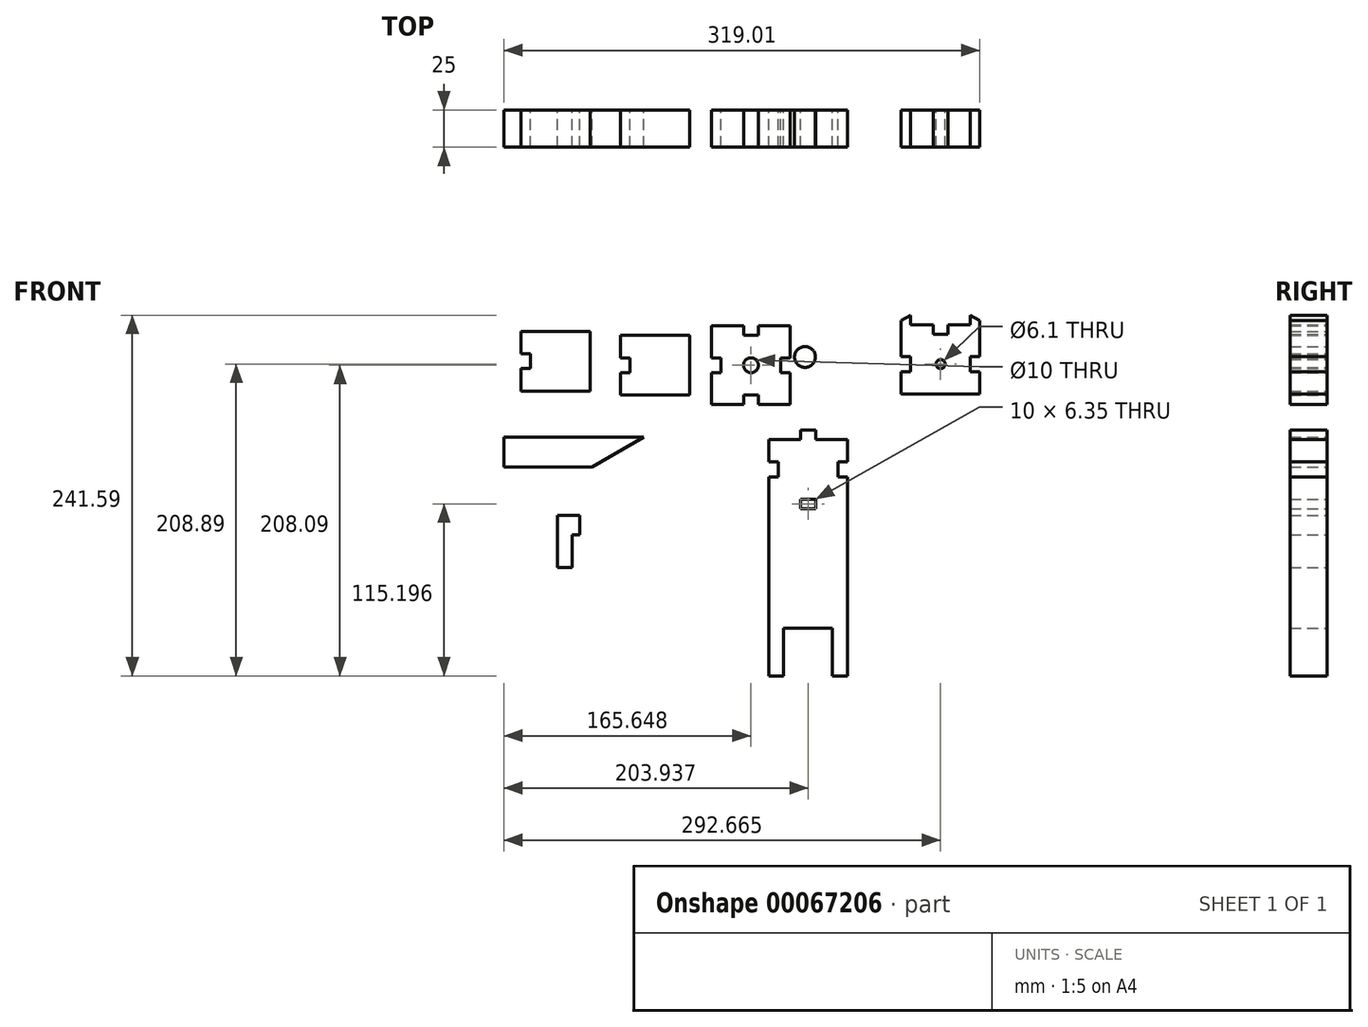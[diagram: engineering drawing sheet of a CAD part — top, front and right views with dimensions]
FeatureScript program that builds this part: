
annotation { "Feature Type Name" : "Feature", "Feature Type Description" : "" }
export const myFeature = defineFeature(function(context is Context, id is Id, definition is map)
    precondition{}
    {
        {
            var Q0;
            Q0=qCreatedBy(makeId("Front.planeOp"),FACE);
            var sketch = newSketch(context, id + "F0", { "sketchPlane" : qUnion([Q0])});
            skLineSegment(sketch, "E0.bottom", {"start": v(-118.5, 6.97) * mm, "end": v(-158.5, 6.97) * mm});
            skLineSegment(sketch, "E0.top", {"start": v(-118.5, 46.97) * mm, "end": v(-158.5, 46.97) * mm});
            skLineSegment(sketch, "E0.left", {"start": v(-118.5, 6.97) * mm, "end": v(-118.5, 46.97) * mm});
            skLineSegment(sketch, "E0.right", {"start": v(-158.5, 6.97) * mm, "end": v(-158.5, 46.97) * mm});
            skPoint(sketch, "E0.middle", {"position": v(-138.5, 26.97) * mm});
            skLineSegment(sketch, "E1.bottom", {"start": v(-112.15, 0.62) * mm, "end": v(-164.85, 0.62) * mm});
            skLineSegment(sketch, "E1.top", {"start": v(-112.15, 53.32) * mm, "end": v(-164.85, 53.32) * mm});
            skLineSegment(sketch, "E1.left", {"start": v(-112.15, 0.62) * mm, "end": v(-112.15, 53.32) * mm});
            skLineSegment(sketch, "E1.right", {"start": v(-164.85, 0.62) * mm, "end": v(-164.85, 53.32) * mm});
            skLineSegment(sketch, "E2.bottom", {"start": v(-133.5, 53.32) * mm, "end": v(-143.5, 53.32) * mm});
            skLineSegment(sketch, "E2.top", {"start": v(-133.5, 40.62) * mm, "end": v(-143.5, 40.62) * mm});
            skLineSegment(sketch, "E2.left", {"start": v(-133.5, 53.32) * mm, "end": v(-133.5, 40.62) * mm});
            skLineSegment(sketch, "E2.right", {"start": v(-143.5, 53.32) * mm, "end": v(-143.5, 40.62) * mm});
            skPoint(sketch, "E2.middle", {"position": v(-138.5, 46.97) * mm});
            skLineSegment(sketch, "E3.bottom", {"start": v(-112.15, 31.97) * mm, "end": v(-124.85, 31.97) * mm});
            skLineSegment(sketch, "E3.top", {"start": v(-112.15, 21.97) * mm, "end": v(-124.85, 21.97) * mm});
            skLineSegment(sketch, "E3.left", {"start": v(-112.15, 31.97) * mm, "end": v(-112.15, 21.97) * mm});
            skLineSegment(sketch, "E3.right", {"start": v(-124.85, 31.97) * mm, "end": v(-124.85, 21.97) * mm});
            skPoint(sketch, "E3.middle", {"position": v(-118.5, 26.97) * mm});
            skLineSegment(sketch, "E4.bottom", {"start": v(-133.5, 0.62) * mm, "end": v(-143.5, 0.62) * mm});
            skLineSegment(sketch, "E4.top", {"start": v(-133.5, 13.32) * mm, "end": v(-143.5, 13.32) * mm});
            skLineSegment(sketch, "E4.left", {"start": v(-133.5, 0.62) * mm, "end": v(-133.5, 13.32) * mm});
            skLineSegment(sketch, "E4.right", {"start": v(-143.5, 0.62) * mm, "end": v(-143.5, 13.32) * mm});
            skPoint(sketch, "E4.middle", {"position": v(-138.5, 6.97) * mm});
            skLineSegment(sketch, "E5.bottom", {"start": v(-164.85, 31.97) * mm, "end": v(-152.15, 31.97) * mm});
            skLineSegment(sketch, "E5.top", {"start": v(-164.85, 21.97) * mm, "end": v(-152.15, 21.97) * mm});
            skLineSegment(sketch, "E5.left", {"start": v(-164.85, 31.97) * mm, "end": v(-164.85, 21.97) * mm});
            skLineSegment(sketch, "E5.right", {"start": v(-152.15, 31.97) * mm, "end": v(-152.15, 21.97) * mm});
            skPoint(sketch, "E5.middle", {"position": v(-158.5, 26.97) * mm});
            skLineSegment(sketch, "E6", {"start": v(-158.5, 46.97) * mm, "end": v(-158.5, 53.32) * mm});
            skLineSegment(sketch, "E7", {"start": v(-158.5, 46.97) * mm, "end": v(-164.85, 46.97) * mm});
            skLineSegment(sketch, "E8", {"start": v(-158.5, 6.97) * mm, "end": v(-164.85, 6.97) * mm});
            skLineSegment(sketch, "E9", {"start": v(-158.5, 6.97) * mm, "end": v(-158.5, 0.62) * mm});
            skLineSegment(sketch, "E10", {"start": v(-118.5, 6.97) * mm, "end": v(-118.5, 0.62) * mm});
            skLineSegment(sketch, "E11", {"start": v(-118.5, 6.97) * mm, "end": v(-112.15, 6.97) * mm});
            skLineSegment(sketch, "E12", {"start": v(-118.5, 46.97) * mm, "end": v(-112.15, 46.97) * mm});
            skLineSegment(sketch, "E13", {"start": v(-118.5, 46.97) * mm, "end": v(-118.5, 53.32) * mm});
            skLineSegment(sketch, "E14.bottom", {"start": v(-51.59, 4.22) * mm, "end": v(-91.59, 4.22) * mm});
            skLineSegment(sketch, "E14.top", {"start": v(-51.59, 44.22) * mm, "end": v(-91.59, 44.22) * mm});
            skLineSegment(sketch, "E14.left", {"start": v(-51.59, 4.22) * mm, "end": v(-51.59, 44.22) * mm});
            skLineSegment(sketch, "E14.right", {"start": v(-91.59, 4.22) * mm, "end": v(-91.59, 44.22) * mm});
            skPoint(sketch, "E14.middle", {"position": v(-71.59, 24.22) * mm});
            skLineSegment(sketch, "E15.bottom", {"start": v(-45.24, -2.13) * mm, "end": v(-97.94, -2.13) * mm});
            skLineSegment(sketch, "E15.top", {"start": v(-45.24, 50.57) * mm, "end": v(-97.94, 50.57) * mm});
            skLineSegment(sketch, "E15.left", {"start": v(-45.24, -2.13) * mm, "end": v(-45.24, 50.57) * mm});
            skLineSegment(sketch, "E15.right", {"start": v(-97.94, -2.13) * mm, "end": v(-97.94, 50.57) * mm});
            skLineSegment(sketch, "E16.bottom", {"start": v(-66.59, 50.57) * mm, "end": v(-76.59, 50.57) * mm});
            skLineSegment(sketch, "E16.top", {"start": v(-66.59, 37.87) * mm, "end": v(-76.59, 37.87) * mm});
            skLineSegment(sketch, "E16.left", {"start": v(-66.59, 50.57) * mm, "end": v(-66.59, 37.87) * mm});
            skLineSegment(sketch, "E16.right", {"start": v(-76.59, 50.57) * mm, "end": v(-76.59, 37.87) * mm});
            skPoint(sketch, "E16.middle", {"position": v(-71.59, 44.22) * mm});
            skLineSegment(sketch, "E17.bottom", {"start": v(-45.24, 29.22) * mm, "end": v(-57.94, 29.22) * mm});
            skLineSegment(sketch, "E17.top", {"start": v(-45.24, 19.22) * mm, "end": v(-57.94, 19.22) * mm});
            skLineSegment(sketch, "E17.left", {"start": v(-45.24, 29.22) * mm, "end": v(-45.24, 19.22) * mm});
            skLineSegment(sketch, "E17.right", {"start": v(-57.94, 29.22) * mm, "end": v(-57.94, 19.22) * mm});
            skPoint(sketch, "E17.middle", {"position": v(-51.59, 24.22) * mm});
            skLineSegment(sketch, "E18.bottom", {"start": v(-66.59, -2.13) * mm, "end": v(-76.59, -2.13) * mm});
            skLineSegment(sketch, "E18.top", {"start": v(-66.59, 10.57) * mm, "end": v(-76.59, 10.57) * mm});
            skLineSegment(sketch, "E18.left", {"start": v(-66.59, -2.13) * mm, "end": v(-66.59, 10.57) * mm});
            skLineSegment(sketch, "E18.right", {"start": v(-76.59, -2.13) * mm, "end": v(-76.59, 10.57) * mm});
            skPoint(sketch, "E18.middle", {"position": v(-71.59, 4.22) * mm});
            skLineSegment(sketch, "E19.bottom", {"start": v(-97.94, 29.22) * mm, "end": v(-85.24, 29.22) * mm});
            skLineSegment(sketch, "E19.top", {"start": v(-97.94, 19.22) * mm, "end": v(-85.24, 19.22) * mm});
            skLineSegment(sketch, "E19.left", {"start": v(-97.94, 29.22) * mm, "end": v(-97.94, 19.22) * mm});
            skLineSegment(sketch, "E19.right", {"start": v(-85.24, 29.22) * mm, "end": v(-85.24, 19.22) * mm});
            skPoint(sketch, "E19.middle", {"position": v(-91.59, 24.22) * mm});
            skLineSegment(sketch, "E20", {"start": v(-91.59, 44.22) * mm, "end": v(-91.59, 50.57) * mm});
            skLineSegment(sketch, "E21", {"start": v(-91.59, 44.22) * mm, "end": v(-97.94, 44.22) * mm});
            skLineSegment(sketch, "E22", {"start": v(-91.59, 4.22) * mm, "end": v(-97.94, 4.22) * mm});
            skLineSegment(sketch, "E23", {"start": v(-91.59, 4.22) * mm, "end": v(-91.59, -2.13) * mm});
            skLineSegment(sketch, "E24", {"start": v(-51.59, 4.22) * mm, "end": v(-51.59, -2.13) * mm});
            skLineSegment(sketch, "E25", {"start": v(-51.59, 4.22) * mm, "end": v(-45.24, 4.22) * mm});
            skLineSegment(sketch, "E26", {"start": v(-51.59, 44.22) * mm, "end": v(-45.24, 44.22) * mm});
            skLineSegment(sketch, "E27", {"start": v(-51.59, 44.22) * mm, "end": v(-51.59, 50.57) * mm});
            skLineSegment(sketch, "E28.bottom", {"start": v(9.4, 4.22) * mm, "end": v(-30.6, 4.22) * mm});
            skLineSegment(sketch, "E28.top", {"start": v(9.4, 44.22) * mm, "end": v(-30.6, 44.22) * mm});
            skLineSegment(sketch, "E28.left", {"start": v(9.4, 4.22) * mm, "end": v(9.4, 44.22) * mm});
            skLineSegment(sketch, "E28.right", {"start": v(-30.6, 4.22) * mm, "end": v(-30.6, 44.22) * mm});
            skPoint(sketch, "E28.middle", {"position": v(-10.6, 24.22) * mm});
            skLineSegment(sketch, "E29.bottom", {"start": v(15.75, -2.13) * mm, "end": v(-36.95, -2.13) * mm});
            skLineSegment(sketch, "E29.top", {"start": v(15.75, 50.57) * mm, "end": v(-36.95, 50.57) * mm});
            skLineSegment(sketch, "E29.left", {"start": v(15.75, -2.13) * mm, "end": v(15.75, 50.57) * mm});
            skLineSegment(sketch, "E29.right", {"start": v(-36.95, -2.13) * mm, "end": v(-36.95, 50.57) * mm});
            skLineSegment(sketch, "E30.bottom", {"start": v(-5.6, 50.57) * mm, "end": v(-15.6, 50.57) * mm});
            skLineSegment(sketch, "E30.top", {"start": v(-5.6, 37.87) * mm, "end": v(-15.6, 37.87) * mm});
            skLineSegment(sketch, "E30.left", {"start": v(-5.6, 50.57) * mm, "end": v(-5.6, 37.87) * mm});
            skLineSegment(sketch, "E30.right", {"start": v(-15.6, 50.57) * mm, "end": v(-15.6, 37.87) * mm});
            skPoint(sketch, "E30.middle", {"position": v(-10.6, 44.22) * mm});
            skLineSegment(sketch, "E31.bottom", {"start": v(15.75, 29.22) * mm, "end": v(3.05, 29.22) * mm});
            skLineSegment(sketch, "E31.top", {"start": v(15.75, 19.22) * mm, "end": v(3.05, 19.22) * mm});
            skLineSegment(sketch, "E31.left", {"start": v(15.75, 29.22) * mm, "end": v(15.75, 19.22) * mm});
            skLineSegment(sketch, "E31.right", {"start": v(3.05, 29.22) * mm, "end": v(3.05, 19.22) * mm});
            skPoint(sketch, "E31.middle", {"position": v(9.4, 24.22) * mm});
            skLineSegment(sketch, "E32.bottom", {"start": v(-5.6, -2.13) * mm, "end": v(-15.6, -2.13) * mm});
            skLineSegment(sketch, "E32.top", {"start": v(-5.6, 10.57) * mm, "end": v(-15.6, 10.57) * mm});
            skLineSegment(sketch, "E32.left", {"start": v(-5.6, -2.13) * mm, "end": v(-5.6, 10.57) * mm});
            skLineSegment(sketch, "E32.right", {"start": v(-15.6, -2.13) * mm, "end": v(-15.6, 10.57) * mm});
            skPoint(sketch, "E32.middle", {"position": v(-10.6, 4.22) * mm});
            skLineSegment(sketch, "E33.bottom", {"start": v(-36.95, 29.22) * mm, "end": v(-24.25, 29.22) * mm});
            skLineSegment(sketch, "E33.top", {"start": v(-36.95, 19.22) * mm, "end": v(-24.25, 19.22) * mm});
            skLineSegment(sketch, "E33.left", {"start": v(-36.95, 29.22) * mm, "end": v(-36.95, 19.22) * mm});
            skLineSegment(sketch, "E33.right", {"start": v(-24.25, 29.22) * mm, "end": v(-24.25, 19.22) * mm});
            skPoint(sketch, "E33.middle", {"position": v(-30.6, 24.22) * mm});
            skLineSegment(sketch, "E34", {"start": v(-30.6, 44.22) * mm, "end": v(-30.6, 50.57) * mm});
            skLineSegment(sketch, "E35", {"start": v(-30.6, 44.22) * mm, "end": v(-36.95, 44.22) * mm});
            skLineSegment(sketch, "E36", {"start": v(-30.6, 4.22) * mm, "end": v(-36.95, 4.22) * mm});
            skLineSegment(sketch, "E37", {"start": v(-30.6, 4.22) * mm, "end": v(-30.6, -2.13) * mm});
            skLineSegment(sketch, "E38", {"start": v(9.4, 4.22) * mm, "end": v(9.4, -2.13) * mm});
            skLineSegment(sketch, "E39", {"start": v(9.4, 4.22) * mm, "end": v(15.75, 4.22) * mm});
            skLineSegment(sketch, "E40", {"start": v(9.4, 44.22) * mm, "end": v(15.75, 44.22) * mm});
            skLineSegment(sketch, "E41", {"start": v(9.4, 44.22) * mm, "end": v(9.4, 50.57) * mm});
            skLineSegment(sketch, "E42.bottom", {"start": v(142.76, -1.33) * mm, "end": v(90.06, -1.33) * mm});
            skLineSegment(sketch, "E42.top", {"start": v(142.76, 51.37) * mm, "end": v(90.06, 51.37) * mm});
            skLineSegment(sketch, "E42.left", {"start": v(142.76, -1.33) * mm, "end": v(142.76, 51.37) * mm});
            skLineSegment(sketch, "E42.right", {"start": v(90.06, -1.33) * mm, "end": v(90.06, 51.37) * mm});
            skPoint(sketch, "E42.middle", {"position": v(116.41, 25.02) * mm});
            skLineSegment(sketch, "E43.bottom", {"start": v(136.41, 5.02) * mm, "end": v(96.41, 5.02) * mm});
            skLineSegment(sketch, "E43.top", {"start": v(136.41, 45.02) * mm, "end": v(96.41, 45.02) * mm});
            skLineSegment(sketch, "E43.left", {"start": v(136.41, 5.02) * mm, "end": v(136.41, 45.02) * mm});
            skLineSegment(sketch, "E43.right", {"start": v(96.41, 5.02) * mm, "end": v(96.41, 45.02) * mm});
            skLineSegment(sketch, "E44.bottom", {"start": v(121.41, 38.53) * mm, "end": v(111.41, 38.53) * mm});
            skLineSegment(sketch, "E44.top", {"start": v(121.41, 51.5) * mm, "end": v(111.41, 51.5) * mm});
            skLineSegment(sketch, "E44.left", {"start": v(121.41, 38.53) * mm, "end": v(121.41, 51.5) * mm});
            skLineSegment(sketch, "E44.right", {"start": v(111.41, 38.53) * mm, "end": v(111.41, 51.5) * mm});
            skPoint(sketch, "E44.middle", {"position": v(116.41, 45.02) * mm});
            skLineSegment(sketch, "E45.bottom", {"start": v(121.41, -1.33) * mm, "end": v(111.41, -1.33) * mm});
            skLineSegment(sketch, "E45.top", {"start": v(121.41, 11.37) * mm, "end": v(111.41, 11.37) * mm});
            skLineSegment(sketch, "E45.left", {"start": v(121.41, -1.33) * mm, "end": v(121.41, 11.37) * mm});
            skLineSegment(sketch, "E45.right", {"start": v(111.41, -1.33) * mm, "end": v(111.41, 11.37) * mm});
            skPoint(sketch, "E45.middle", {"position": v(116.41, 5.02) * mm});
            skLineSegment(sketch, "E46.bottom", {"start": v(142.76, 20.02) * mm, "end": v(130.06, 20.02) * mm});
            skLineSegment(sketch, "E46.top", {"start": v(142.76, 30.02) * mm, "end": v(130.06, 30.02) * mm});
            skLineSegment(sketch, "E46.left", {"start": v(142.76, 20.02) * mm, "end": v(142.76, 30.02) * mm});
            skLineSegment(sketch, "E46.right", {"start": v(130.06, 20.02) * mm, "end": v(130.06, 30.02) * mm});
            skPoint(sketch, "E46.middle", {"position": v(136.41, 25.02) * mm});
            skLineSegment(sketch, "E47.bottom", {"start": v(90.06, 20.02) * mm, "end": v(102.76, 20.02) * mm});
            skLineSegment(sketch, "E47.top", {"start": v(90.06, 30.02) * mm, "end": v(102.76, 30.02) * mm});
            skLineSegment(sketch, "E47.left", {"start": v(90.06, 20.02) * mm, "end": v(90.06, 30.02) * mm});
            skLineSegment(sketch, "E47.right", {"start": v(102.76, 20.02) * mm, "end": v(102.76, 30.02) * mm});
            skPoint(sketch, "E47.middle", {"position": v(96.41, 25.02) * mm});
            skLineSegment(sketch, "E48.bottom", {"start": v(90.06, 51.37) * mm, "end": v(142.76, 51.37) * mm});
            skLineSegment(sketch, "E48.top", {"start": v(90.06, 57.72) * mm, "end": v(142.76, 57.72) * mm});
            skLineSegment(sketch, "E48.left", {"start": v(90.06, 51.37) * mm, "end": v(90.06, 57.72) * mm});
            skLineSegment(sketch, "E48.right", {"start": v(142.76, 51.37) * mm, "end": v(142.76, 57.72) * mm});
            skLineSegment(sketch, "E49", {"start": v(96.41, 45.02) * mm, "end": v(96.41, 57.72) * mm});
            skLineSegment(sketch, "E50", {"start": v(136.41, 45.02) * mm, "end": v(136.41, 57.72) * mm});
            skLineSegment(sketch, "E51", {"start": v(96.41, 5.02) * mm, "end": v(90.06, 5.02) * mm});
            skLineSegment(sketch, "E52", {"start": v(96.41, 5.02) * mm, "end": v(96.41, -1.33) * mm});
            skLineSegment(sketch, "E53", {"start": v(136.41, 5.02) * mm, "end": v(136.41, -1.33) * mm});
            skLineSegment(sketch, "E54", {"start": v(136.41, 5.02) * mm, "end": v(142.76, 5.02) * mm});
            skCircle(sketch, "E55", {"center": v(116.41, 25.02) * mm, "radius": 3.05 * mm});
            skLineSegment(sketch, "E56", {"start": v(90.06, 54.05) * mm, "end": v(96.41, 57.72) * mm});
            skLineSegment(sketch, "E57", {"start": v(142.76, 54.05) * mm, "end": v(136.41, 57.72) * mm});
            skLineSegment(sketch, "E58.left", {"start": v(1.4, -25.5) * mm, "end": v(1.21, -183.85) * mm});
            skLineSegment(sketch, "E58.right", {"start": v(54.1, -25.52) * mm, "end": v(53.91, -183.87) * mm});
            skLineSegment(sketch, "E59.top", {"start": v(11.21, -151.85) * mm, "end": v(43.91, -151.85) * mm});
            skLineSegment(sketch, "E59.left", {"start": v(11.21, -183.85) * mm, "end": v(11.21, -151.85) * mm});
            skLineSegment(sketch, "E59.right", {"start": v(43.91, -183.85) * mm, "end": v(43.91, -151.85) * mm});
            skLineSegment(sketch, "E60", {"start": v(11.21, -183.85) * mm, "end": v(1.21, -183.85) * mm});
            skLineSegment(sketch, "E61", {"start": v(53.91, -183.87) * mm, "end": v(43.91, -183.85) * mm});
            skPoint(sketch, "E62.centerSnap0", {"position": v(27.75, -25.5) * mm});
            skLineSegment(sketch, "E63", {"start": v(27.75, -25.5) * mm, "end": v(27.56, -151.85) * mm});
            skLineSegment(sketch, "E64.bottom", {"start": v(32.75, -19.16) * mm, "end": v(22.75, -19.16) * mm});
            skLineSegment(sketch, "E64.left", {"start": v(32.75, -19.16) * mm, "end": v(32.75, -31.86) * mm});
            skLineSegment(sketch, "E64.right", {"start": v(22.75, -19.16) * mm, "end": v(22.75, -31.86) * mm});
            skCircle(sketch, "E65", {"center": v(-10.6, 24.22) * mm, "radius": 5 * mm});
            skCircle(sketch, "E66", {"center": v(25.58, 29.76) * mm, "radius": 7 * mm});
            skLineSegment(sketch, "E67.top", {"start": v(7.72, -65.5) * mm, "end": v(47.72, -65.5) * mm});
            skLineSegment(sketch, "E67.right", {"start": v(47.72, -25.5) * mm, "end": v(47.72, -65.5) * mm});
            skPoint(sketch, "E67.middle", {"position": v(27.72, -45.5) * mm});
            skLineSegment(sketch, "E68.bottom", {"start": v(1.38, -40.5) * mm, "end": v(14.06, -40.5) * mm});
            skLineSegment(sketch, "E68.right", {"start": v(14.06, -40.5) * mm, "end": v(14.05, -50.5) * mm});
            skPoint(sketch, "E68.middle", {"position": v(7.72, -45.5) * mm});
            skLineSegment(sketch, "E69.bottom", {"start": v(54.08, -40.5) * mm, "end": v(41.35, -40.5) * mm});
            skLineSegment(sketch, "E69.top", {"start": v(54.08, -50.5) * mm, "end": v(41.35, -50.5) * mm});
            skLineSegment(sketch, "E69.right", {"start": v(41.35, -40.5) * mm, "end": v(41.35, -50.5) * mm});
            skPoint(sketch, "E69.middle", {"position": v(47.72, -45.5) * mm});
            skLineSegment(sketch, "E70.bottom", {"start": v(32.69, -71.85) * mm, "end": v(22.69, -71.85) * mm});
            skLineSegment(sketch, "E70.top", {"start": v(32.69, -59.15) * mm, "end": v(22.69, -59.15) * mm});
            skLineSegment(sketch, "E70.left", {"start": v(32.69, -71.85) * mm, "end": v(32.69, -59.15) * mm});
            skLineSegment(sketch, "E70.right", {"start": v(22.69, -71.85) * mm, "end": v(22.69, -59.15) * mm});
            skPoint(sketch, "E70.middle", {"position": v(27.69, -65.5) * mm});
            skPoint(sketch, "E70.middle.positionSnap0", {"position": v(27.72, -65.5) * mm});
            skPoint(sketch, "E70.centerSnap0", {"position": v(27.72, -65.5) * mm});
            skLineSegment(sketch, "E71", {"start": v(32.75, -25.5) * mm, "end": v(54.1, -25.52) * mm});
            skLineSegment(sketch, "E72", {"start": v(22.75, -25.5) * mm, "end": v(1.4, -25.5) * mm});
            skLineSegment(sketch, "E73", {"start": v(14.05, -50.5) * mm, "end": v(1.37, -50.5) * mm});
            skLineSegment(sketch, "E74", {"start": v(7.72, -65.5) * mm, "end": v(7.72, -25.5) * mm});
            skLineSegment(sketch, "E75.bottom", {"start": v(-82.56, -44.05) * mm, "end": v(-176.25, -44.05) * mm});
            skLineSegment(sketch, "E75.top", {"start": v(-82.56, -24.05) * mm, "end": v(-176.25, -24.05) * mm});
            skLineSegment(sketch, "E75.left", {"start": v(-82.56, -44.05) * mm, "end": v(-82.56, -24.05) * mm});
            skLineSegment(sketch, "E75.right", {"start": v(-176.25, -44.05) * mm, "end": v(-176.25, -24.05) * mm});
            skPoint(sketch, "E75.middle", {"position": v(-129.4, -34.05) * mm});
            skLineSegment(sketch, "E76", {"start": v(-117.2, -44.05) * mm, "end": v(-82.56, -24.05) * mm});
            skLineSegment(sketch, "E77.bottom", {"start": v(-130.39, -111.38) * mm, "end": v(-140.39, -111.38) * mm});
            skLineSegment(sketch, "E77.top", {"start": v(-130.39, -76.38) * mm, "end": v(-140.39, -76.38) * mm});
            skLineSegment(sketch, "E77.left", {"start": v(-130.39, -111.38) * mm, "end": v(-130.39, -76.38) * mm});
            skLineSegment(sketch, "E77.right", {"start": v(-140.39, -111.38) * mm, "end": v(-140.39, -76.38) * mm});
            skPoint(sketch, "E77.middle", {"position": v(-135.39, -93.88) * mm});
            skLineSegment(sketch, "E78.bottom", {"start": v(-130.39, -76.38) * mm, "end": v(-125.39, -76.38) * mm});
            skLineSegment(sketch, "E78.top", {"start": v(-130.39, -89.38) * mm, "end": v(-125.39, -89.38) * mm});
            skLineSegment(sketch, "E78.left", {"start": v(-130.39, -76.38) * mm, "end": v(-130.39, -89.38) * mm});
            skLineSegment(sketch, "E78.right", {"start": v(-125.39, -76.38) * mm, "end": v(-125.39, -89.38) * mm});
            skSolve(sketch);
        }
        {
            var Q0;
            {var subQ0=sQuery(id+"F0.wireOp",EDGE,"E72");var subQ1=sQuery(id+"F0.wireOp",EDGE,"E58.left");var subQ2=makeQuery(id+"F0.imprint","INTERSECT",VERTEX,{"derivedFrom":[subQ1,subQ0]});Q0=makeQuery(id+"F0.imprint","IMPRINT",FACE,{"disambiguationData":[TD([[makeQuery(id+"F0.imprint","IMPRINT",EDGE,{"disambiguationData":[TD([[subQ2,-1.0]])],"derivedFrom":subQ1}),1.0]])]});}
            var Q1;
            {var subQ10=sQuery(id+"F0.wireOp",EDGE,"E2.top");Q1=makeQuery(id+"F0.imprint","IMPRINT",FACE,{"disambiguationData":[TD([[makeQuery(id+"F0.imprint","IMPRINT",EDGE,{"derivedFrom":subQ10}),1.0]])]});}
            var Q2;
            {var subQ5=sQuery(id+"F0.wireOp",EDGE,"E5.right");Q2=makeQuery(id+"F0.imprint","IMPRINT",FACE,{"disambiguationData":[TD([[makeQuery(id+"F0.imprint","IMPRINT",EDGE,{"derivedFrom":subQ5}),-1.0]])]});}
            var Q3;
            {var subQ5=sQuery(id+"F0.wireOp",EDGE,"E4.top");Q3=makeQuery(id+"F0.imprint","IMPRINT",FACE,{"disambiguationData":[TD([[makeQuery(id+"F0.imprint","IMPRINT",EDGE,{"derivedFrom":subQ5}),1.0]])]});}
            var Q4;
            {var subQ5=sQuery(id+"F0.wireOp",EDGE,"E3.right");Q4=makeQuery(id+"F0.imprint","IMPRINT",FACE,{"disambiguationData":[TD([[makeQuery(id+"F0.imprint","IMPRINT",EDGE,{"derivedFrom":subQ5}),1.0]])]});}
            var Q5;
            {var subQ5=sQuery(id+"F0.wireOp",EDGE,"E2.top");Q5=makeQuery(id+"F0.imprint","IMPRINT",FACE,{"disambiguationData":[TD([[makeQuery(id+"F0.imprint","IMPRINT",EDGE,{"derivedFrom":subQ5}),-1.0]])]});}
            var Q6;
            {var subQ5=sQuery(id+"F0.wireOp",EDGE,"E4.bottom");Q6=makeQuery(id+"F0.imprint","IMPRINT",FACE,{"disambiguationData":[TD([[makeQuery(id+"F0.imprint","IMPRINT",EDGE,{"derivedFrom":subQ5}),-1.0]])]});}
            var Q7;
            {var subQ0=sQuery(id+"F0.wireOp",EDGE,"E7");Q7=makeQuery(id+"F0.imprint","IMPRINT",FACE,{"disambiguationData":[TD([[makeQuery(id+"F0.imprint","IMPRINT",EDGE,{"derivedFrom":subQ0}),1.0]])]});}
            var Q8;
            {var subQ0=sQuery(id+"F0.wireOp",EDGE,"E8");Q8=makeQuery(id+"F0.imprint","IMPRINT",FACE,{"disambiguationData":[TD([[makeQuery(id+"F0.imprint","IMPRINT",EDGE,{"derivedFrom":subQ0}),-1.0]])]});}
            var Q9;
            {var subQ5=sQuery(id+"F0.wireOp",EDGE,"E2.bottom");Q9=makeQuery(id+"F0.imprint","IMPRINT",FACE,{"disambiguationData":[TD([[makeQuery(id+"F0.imprint","IMPRINT",EDGE,{"derivedFrom":subQ5}),1.0]])]});}
            var Q10;
            {var subQ5=sQuery(id+"F0.wireOp",EDGE,"E3.left");Q10=makeQuery(id+"F0.imprint","IMPRINT",FACE,{"disambiguationData":[TD([[makeQuery(id+"F0.imprint","IMPRINT",EDGE,{"derivedFrom":subQ5}),-1.0]])]});}
            var Q11;
            {var subQ0=sQuery(id+"F0.wireOp",EDGE,"E21");Q11=makeQuery(id+"F0.imprint","IMPRINT",FACE,{"disambiguationData":[TD([[makeQuery(id+"F0.imprint","IMPRINT",EDGE,{"derivedFrom":subQ0}),1.0]])]});}
            var Q12;
            {var subQ0=sQuery(id+"F0.wireOp",EDGE,"E22");Q12=makeQuery(id+"F0.imprint","IMPRINT",FACE,{"disambiguationData":[TD([[makeQuery(id+"F0.imprint","IMPRINT",EDGE,{"derivedFrom":subQ0}),-1.0]])]});}
            var Q13;
            {var subQ0=sQuery(id+"F0.wireOp",EDGE,"E16.top");Q13=makeQuery(id+"F0.imprint","IMPRINT",FACE,{"disambiguationData":[TD([[makeQuery(id+"F0.imprint","IMPRINT",EDGE,{"derivedFrom":subQ0}),1.0]])]});}
            var Q14;
            {var subQ5=sQuery(id+"F0.wireOp",EDGE,"E16.top");Q14=makeQuery(id+"F0.imprint","IMPRINT",FACE,{"disambiguationData":[TD([[makeQuery(id+"F0.imprint","IMPRINT",EDGE,{"derivedFrom":subQ5}),-1.0]])]});}
            var Q15;
            {var subQ5=sQuery(id+"F0.wireOp",EDGE,"E16.bottom");Q15=makeQuery(id+"F0.imprint","IMPRINT",FACE,{"disambiguationData":[TD([[makeQuery(id+"F0.imprint","IMPRINT",EDGE,{"derivedFrom":subQ5}),1.0]])]});}
            var Q16;
            {var subQ5=sQuery(id+"F0.wireOp",EDGE,"E17.right");Q16=makeQuery(id+"F0.imprint","IMPRINT",FACE,{"disambiguationData":[TD([[makeQuery(id+"F0.imprint","IMPRINT",EDGE,{"derivedFrom":subQ5}),1.0]])]});}
            var Q17;
            {var subQ5=sQuery(id+"F0.wireOp",EDGE,"E17.left");Q17=makeQuery(id+"F0.imprint","IMPRINT",FACE,{"disambiguationData":[TD([[makeQuery(id+"F0.imprint","IMPRINT",EDGE,{"derivedFrom":subQ5}),-1.0]])]});}
            var Q18;
            {var subQ5=sQuery(id+"F0.wireOp",EDGE,"E18.top");Q18=makeQuery(id+"F0.imprint","IMPRINT",FACE,{"disambiguationData":[TD([[makeQuery(id+"F0.imprint","IMPRINT",EDGE,{"derivedFrom":subQ5}),1.0]])]});}
            var Q19;
            {var subQ5=sQuery(id+"F0.wireOp",EDGE,"E18.bottom");Q19=makeQuery(id+"F0.imprint","IMPRINT",FACE,{"disambiguationData":[TD([[makeQuery(id+"F0.imprint","IMPRINT",EDGE,{"derivedFrom":subQ5}),-1.0]])]});}
            var Q20;
            {var subQ10=sQuery(id+"F0.wireOp",EDGE,"E30.top");Q20=makeQuery(id+"F0.imprint","IMPRINT",FACE,{"disambiguationData":[TD([[makeQuery(id+"F0.imprint","IMPRINT",EDGE,{"derivedFrom":subQ10}),1.0]])]});}
            var Q21;
            {var subQ5=sQuery(id+"F0.wireOp",EDGE,"E33.right");Q21=makeQuery(id+"F0.imprint","IMPRINT",FACE,{"disambiguationData":[TD([[makeQuery(id+"F0.imprint","IMPRINT",EDGE,{"derivedFrom":subQ5}),-1.0]])]});}
            var Q22;
            {var subQ0=sQuery(id+"F0.wireOp",EDGE,"E36");Q22=makeQuery(id+"F0.imprint","IMPRINT",FACE,{"disambiguationData":[TD([[makeQuery(id+"F0.imprint","IMPRINT",EDGE,{"derivedFrom":subQ0}),-1.0]])]});}
            var Q23;
            {var subQ5=sQuery(id+"F0.wireOp",EDGE,"E31.right");Q23=makeQuery(id+"F0.imprint","IMPRINT",FACE,{"disambiguationData":[TD([[makeQuery(id+"F0.imprint","IMPRINT",EDGE,{"derivedFrom":subQ5}),1.0]])]});}
            var Q24;
            {var subQ5=sQuery(id+"F0.wireOp",EDGE,"E30.top");Q24=makeQuery(id+"F0.imprint","IMPRINT",FACE,{"disambiguationData":[TD([[makeQuery(id+"F0.imprint","IMPRINT",EDGE,{"derivedFrom":subQ5}),-1.0]])]});}
            var Q25;
            {var subQ5=sQuery(id+"F0.wireOp",EDGE,"E32.top");Q25=makeQuery(id+"F0.imprint","IMPRINT",FACE,{"disambiguationData":[TD([[makeQuery(id+"F0.imprint","IMPRINT",EDGE,{"derivedFrom":subQ5}),1.0]])]});}
            var Q26;
            {var subQ3=sQuery(id+"F0.wireOp",EDGE,"E34");Q26=makeQuery(id+"F0.imprint","IMPRINT",FACE,{"disambiguationData":[TD([[makeQuery(id+"F0.imprint","IMPRINT",EDGE,{"derivedFrom":subQ3}),1.0]])]});}
            var Q27;
            {var subQ0=sQuery(id+"F0.wireOp",EDGE,"E35");Q27=makeQuery(id+"F0.imprint","IMPRINT",FACE,{"disambiguationData":[TD([[makeQuery(id+"F0.imprint","IMPRINT",EDGE,{"derivedFrom":subQ0}),1.0]])]});}
            var Q28;
            {var subQ0=sQuery(id+"F0.wireOp",EDGE,"E34");Q28=makeQuery(id+"F0.imprint","IMPRINT",FACE,{"disambiguationData":[TD([[makeQuery(id+"F0.imprint","IMPRINT",EDGE,{"derivedFrom":subQ0}),-1.0]])]});}
            var Q29;
            {var subQ0=sQuery(id+"F0.wireOp",EDGE,"E41");Q29=makeQuery(id+"F0.imprint","IMPRINT",FACE,{"disambiguationData":[TD([[makeQuery(id+"F0.imprint","IMPRINT",EDGE,{"derivedFrom":subQ0}),1.0]])]});}
            var Q30;
            {var subQ4=sQuery(id+"F0.wireOp",EDGE,"E40");Q30=makeQuery(id+"F0.imprint","IMPRINT",FACE,{"disambiguationData":[TD([[makeQuery(id+"F0.imprint","IMPRINT",EDGE,{"derivedFrom":subQ4}),1.0]])]});}
            var Q31;
            {var subQ0=sQuery(id+"F0.wireOp",EDGE,"E40");Q31=makeQuery(id+"F0.imprint","IMPRINT",FACE,{"disambiguationData":[TD([[makeQuery(id+"F0.imprint","IMPRINT",EDGE,{"derivedFrom":subQ0}),-1.0]])]});}
            var Q32;
            {var subQ0=sQuery(id+"F0.wireOp",EDGE,"E39");Q32=makeQuery(id+"F0.imprint","IMPRINT",FACE,{"disambiguationData":[TD([[makeQuery(id+"F0.imprint","IMPRINT",EDGE,{"derivedFrom":subQ0}),1.0]])]});}
            var Q33;
            {var subQ3=sQuery(id+"F0.wireOp",EDGE,"E38");Q33=makeQuery(id+"F0.imprint","IMPRINT",FACE,{"disambiguationData":[TD([[makeQuery(id+"F0.imprint","IMPRINT",EDGE,{"derivedFrom":subQ3}),1.0]])]});}
            var Q34;
            {var subQ0=sQuery(id+"F0.wireOp",EDGE,"E38");Q34=makeQuery(id+"F0.imprint","IMPRINT",FACE,{"disambiguationData":[TD([[makeQuery(id+"F0.imprint","IMPRINT",EDGE,{"derivedFrom":subQ0}),-1.0]])]});}
            var Q35;
            {var subQ0=sQuery(id+"F0.wireOp",EDGE,"E37");Q35=makeQuery(id+"F0.imprint","IMPRINT",FACE,{"disambiguationData":[TD([[makeQuery(id+"F0.imprint","IMPRINT",EDGE,{"derivedFrom":subQ0}),1.0]])]});}
            var Q36;
            {var subQ4=sQuery(id+"F0.wireOp",EDGE,"E36");Q36=makeQuery(id+"F0.imprint","IMPRINT",FACE,{"disambiguationData":[TD([[makeQuery(id+"F0.imprint","IMPRINT",EDGE,{"derivedFrom":subQ4}),1.0]])]});}
            var Q37;
            {var subQ5=sQuery(id+"F0.wireOp",EDGE,"E45.bottom");Q37=makeQuery(id+"F0.imprint","IMPRINT",FACE,{"disambiguationData":[TD([[makeQuery(id+"F0.imprint","IMPRINT",EDGE,{"derivedFrom":subQ5}),-1.0]])]});}
            var Q38;
            {var subQ5=sQuery(id+"F0.wireOp",EDGE,"E45.top");Q38=makeQuery(id+"F0.imprint","IMPRINT",FACE,{"disambiguationData":[TD([[makeQuery(id+"F0.imprint","IMPRINT",EDGE,{"derivedFrom":subQ5}),1.0]])]});}
            var Q39;
            {var subQ1=sQuery(id+"F0.wireOp",EDGE,"E44.bottom");Q39=makeQuery(id+"F0.imprint","IMPRINT",FACE,{"disambiguationData":[TD([[makeQuery(id+"F0.imprint","IMPRINT",EDGE,{"derivedFrom":subQ1}),1.0]])]});}
            var Q40;
            {var subQ3=sQuery(id+"F0.wireOp",EDGE,"E51");Q40=makeQuery(id+"F0.imprint","IMPRINT",FACE,{"disambiguationData":[TD([[makeQuery(id+"F0.imprint","IMPRINT",EDGE,{"derivedFrom":subQ3}),-1.0]])]});}
            var Q41;
            {var subQ5=sQuery(id+"F0.wireOp",EDGE,"E47.right");Q41=makeQuery(id+"F0.imprint","IMPRINT",FACE,{"disambiguationData":[TD([[makeQuery(id+"F0.imprint","IMPRINT",EDGE,{"derivedFrom":subQ5}),1.0]])]});}
            var Q42;
            {var subQ5=sQuery(id+"F0.wireOp",EDGE,"E47.top");var subQ7=sQuery(id+"F0.wireOp",EDGE,"E43.right");var subQ8=makeQuery(id+"F0.imprint","INTERSECT",VERTEX,{"derivedFrom":[subQ7,subQ5]});Q42=makeQuery(id+"F0.imprint","IMPRINT",FACE,{"disambiguationData":[TD([[makeQuery(id+"F0.imprint","IMPRINT",EDGE,{"disambiguationData":[TD([[subQ8,-1.0]])],"derivedFrom":subQ7}),1.0]])]});}
            var Q43;
            {var subQ5=sQuery(id+"F0.wireOp",EDGE,"E44.bottom");Q43=makeQuery(id+"F0.imprint","IMPRINT",FACE,{"disambiguationData":[TD([[makeQuery(id+"F0.imprint","IMPRINT",EDGE,{"derivedFrom":subQ5}),-1.0]])]});}
            var Q44;
            {var subQ1=sQuery(id+"F0.wireOp",EDGE,"E43.top");var subQ3=sQuery(id+"F0.wireOp",EDGE,"E44.right");var subQ4=makeQuery(id+"F0.imprint","INTERSECT",VERTEX,{"derivedFrom":[subQ1,subQ3]});Q44=makeQuery(id+"F0.imprint","IMPRINT",FACE,{"disambiguationData":[TD([[makeQuery(id+"F0.imprint","IMPRINT",EDGE,{"disambiguationData":[TD([[subQ4,-1.0]])],"derivedFrom":subQ3}),1.0]])]});}
            var Q45;
            {var subQ1=sQuery(id+"F0.wireOp",EDGE,"E43.top");var subQ3=sQuery(id+"F0.wireOp",EDGE,"E44.left");var subQ4=makeQuery(id+"F0.imprint","INTERSECT",VERTEX,{"derivedFrom":[subQ1,subQ3]});Q45=makeQuery(id+"F0.imprint","IMPRINT",FACE,{"disambiguationData":[TD([[makeQuery(id+"F0.imprint","IMPRINT",EDGE,{"disambiguationData":[TD([[subQ4,-1.0]])],"derivedFrom":subQ3}),-1.0]])]});}
            var Q46;
            {var subQ5=sQuery(id+"F0.wireOp",EDGE,"E46.right");Q46=makeQuery(id+"F0.imprint","IMPRINT",FACE,{"disambiguationData":[TD([[makeQuery(id+"F0.imprint","IMPRINT",EDGE,{"derivedFrom":subQ5}),-1.0]])]});}
            var Q47;
            {var subQ3=sQuery(id+"F0.wireOp",EDGE,"E54");Q47=makeQuery(id+"F0.imprint","IMPRINT",FACE,{"disambiguationData":[TD([[makeQuery(id+"F0.imprint","IMPRINT",EDGE,{"derivedFrom":subQ3}),1.0]])]});}
            var Q48;
            {var subQ1=sQuery(id+"F0.wireOp",EDGE,"E43.left");var subQ3=sQuery(id+"F0.wireOp",EDGE,"E46.top");var subQ4=makeQuery(id+"F0.imprint","INTERSECT",VERTEX,{"derivedFrom":[subQ1,subQ3]});Q48=makeQuery(id+"F0.imprint","IMPRINT",FACE,{"disambiguationData":[TD([[makeQuery(id+"F0.imprint","IMPRINT",EDGE,{"disambiguationData":[TD([[subQ4,-1.0]])],"derivedFrom":subQ1}),-1.0]])]});}
            var Q49;
            {var subQ5=sQuery(id+"F0.wireOp",EDGE,"E57");Q49=makeQuery(id+"F0.imprint","IMPRINT",FACE,{"disambiguationData":[TD([[makeQuery(id+"F0.imprint","IMPRINT",EDGE,{"derivedFrom":subQ5}),1.0]])]});}
            var Q50;
            {var subQ5=sQuery(id+"F0.wireOp",EDGE,"E56");Q50=makeQuery(id+"F0.imprint","IMPRINT",FACE,{"disambiguationData":[TD([[makeQuery(id+"F0.imprint","IMPRINT",EDGE,{"derivedFrom":subQ5}),-1.0]])]});}
            var Q51;
            {var subQ5=sQuery(id+"F0.wireOp",EDGE,"E19.right");Q51=makeQuery(id+"F0.imprint","IMPRINT",FACE,{"disambiguationData":[TD([[makeQuery(id+"F0.imprint","IMPRINT",EDGE,{"derivedFrom":subQ5}),-1.0]])]});}
            var Q52;
            {var subQ1=sQuery(id+"F0.wireOp",EDGE,"E59.right");Q52=makeQuery(id+"F0.imprint","IMPRINT",FACE,{"disambiguationData":[TD([[makeQuery(id+"F0.imprint","IMPRINT",EDGE,{"derivedFrom":subQ1}),-1.0]])]});}
            var Q53;
            Q53=makeQuery(id+"F0.imprint","IMPRINT",FACE,{"disambiguationData":[TD([[makeQuery(id+"F0.imprint","IMPRINT",EDGE,{"derivedFrom":sQuery(id+"F0.wireOp",EDGE,"E66")}),1.0]])]});
            var Q54;
            {var subQ5=sQuery(id+"F0.wireOp",EDGE,"E69.right");Q54=makeQuery(id+"F0.imprint","IMPRINT",FACE,{"disambiguationData":[TD([[makeQuery(id+"F0.imprint","IMPRINT",EDGE,{"derivedFrom":subQ5}),1.0]])]});}
            var Q55;
            {var subQ0=sQuery(id+"F0.wireOp",EDGE,"E68.right");Q55=makeQuery(id+"F0.imprint","IMPRINT",FACE,{"disambiguationData":[TD([[makeQuery(id+"F0.imprint","IMPRINT",EDGE,{"derivedFrom":subQ0}),-1.0]])]});}
            var Q56;
            {var subQ18=sQuery(id+"F0.wireOp",EDGE,"E64.bottom");Q56=makeQuery(id+"F0.imprint","IMPRINT",FACE,{"disambiguationData":[TD([[makeQuery(id+"F0.imprint","IMPRINT",EDGE,{"derivedFrom":subQ18}),1.0]])]});}
            var Q57;
            {var subQ0=sQuery(id+"F0.wireOp",EDGE,"E70.top");var subQ1=sQuery(id+"F0.wireOp",EDGE,"E63");var subQ2=makeQuery(id+"F0.imprint","INTERSECT",VERTEX,{"derivedFrom":[subQ1,subQ0]});Q57=makeQuery(id+"F0.imprint","IMPRINT",FACE,{"disambiguationData":[TD([[makeQuery(id+"F0.imprint","IMPRINT",EDGE,{"disambiguationData":[TD([[subQ2,-1.0]])],"derivedFrom":subQ1}),1.0]])]});}
            var Q58;
            {var subQ0=sQuery(id+"F0.wireOp",EDGE,"E70.top");var subQ1=sQuery(id+"F0.wireOp",EDGE,"E63");var subQ2=makeQuery(id+"F0.imprint","INTERSECT",VERTEX,{"derivedFrom":[subQ1,subQ0]});Q58=makeQuery(id+"F0.imprint","IMPRINT",FACE,{"disambiguationData":[TD([[makeQuery(id+"F0.imprint","IMPRINT",EDGE,{"disambiguationData":[TD([[subQ2,-1.0]])],"derivedFrom":subQ1}),-1.0]])]});}
            var Q59;
            {var subQ11=sQuery(id+"F0.wireOp",EDGE,"E59.left");Q59=makeQuery(id+"F0.imprint","IMPRINT",FACE,{"disambiguationData":[TD([[makeQuery(id+"F0.imprint","IMPRINT",EDGE,{"derivedFrom":subQ11}),1.0]])]});}
            var Q60;
            {var subQ0=sQuery(id+"F0.wireOp",EDGE,"E71");var subQ1=sQuery(id+"F0.wireOp",EDGE,"E58.right");var subQ2=makeQuery(id+"F0.imprint","INTERSECT",VERTEX,{"derivedFrom":[subQ1,subQ0]});Q60=makeQuery(id+"F0.imprint","IMPRINT",FACE,{"disambiguationData":[TD([[makeQuery(id+"F0.imprint","IMPRINT",EDGE,{"disambiguationData":[TD([[subQ2,-1.0]])],"derivedFrom":subQ1}),-1.0]])]});}
            var Q61;
            Q61=makeQuery(id+"F0.imprint","IMPRINT",FACE,{"disambiguationData":[TD([[makeQuery(id+"F0.imprint","IMPRINT",EDGE,{"derivedFrom":sQuery(id+"F0.wireOp",EDGE,"E75.top")}),1.0]])]});
            var Q62;
            Q62=makeQuery(id+"F0.imprint","IMPRINT",FACE,{"disambiguationData":[TD([[makeQuery(id+"F0.imprint","IMPRINT",EDGE,{"derivedFrom":sQuery(id+"F0.wireOp",EDGE,"E77.bottom")}),-1.0]])]});
            var Q63;
            Q63=makeQuery(id+"F0.imprint","IMPRINT",FACE,{"disambiguationData":[TD([[makeQuery(id+"F0.imprint","IMPRINT",EDGE,{"derivedFrom":sQuery(id+"F0.wireOp",EDGE,"E78.bottom")}),-1.0]])]});
            extrude(context, id + "F1", {"entities" : qUnion([Q0, Q1, Q2, Q3, Q4, Q5, Q6, Q7, Q8, Q9, Q10, Q11, Q12, Q13, Q14, Q15, Q16, Q17, Q18, Q19, Q20, Q21, Q22, Q23, Q24, Q25, Q26, Q27, Q28, Q29, Q30, Q31, Q32, Q33, Q34, Q35, Q36, Q37, Q38, Q39, Q40, Q41, Q42, Q43, Q44, Q45, Q46, Q47, Q48, Q49, Q50, Q51, Q52, Q53, Q54, Q55, Q56, Q57, Q58, Q59, Q60, Q61, Q62, Q63]), "depth" : 25 * mm});
        }
    });
